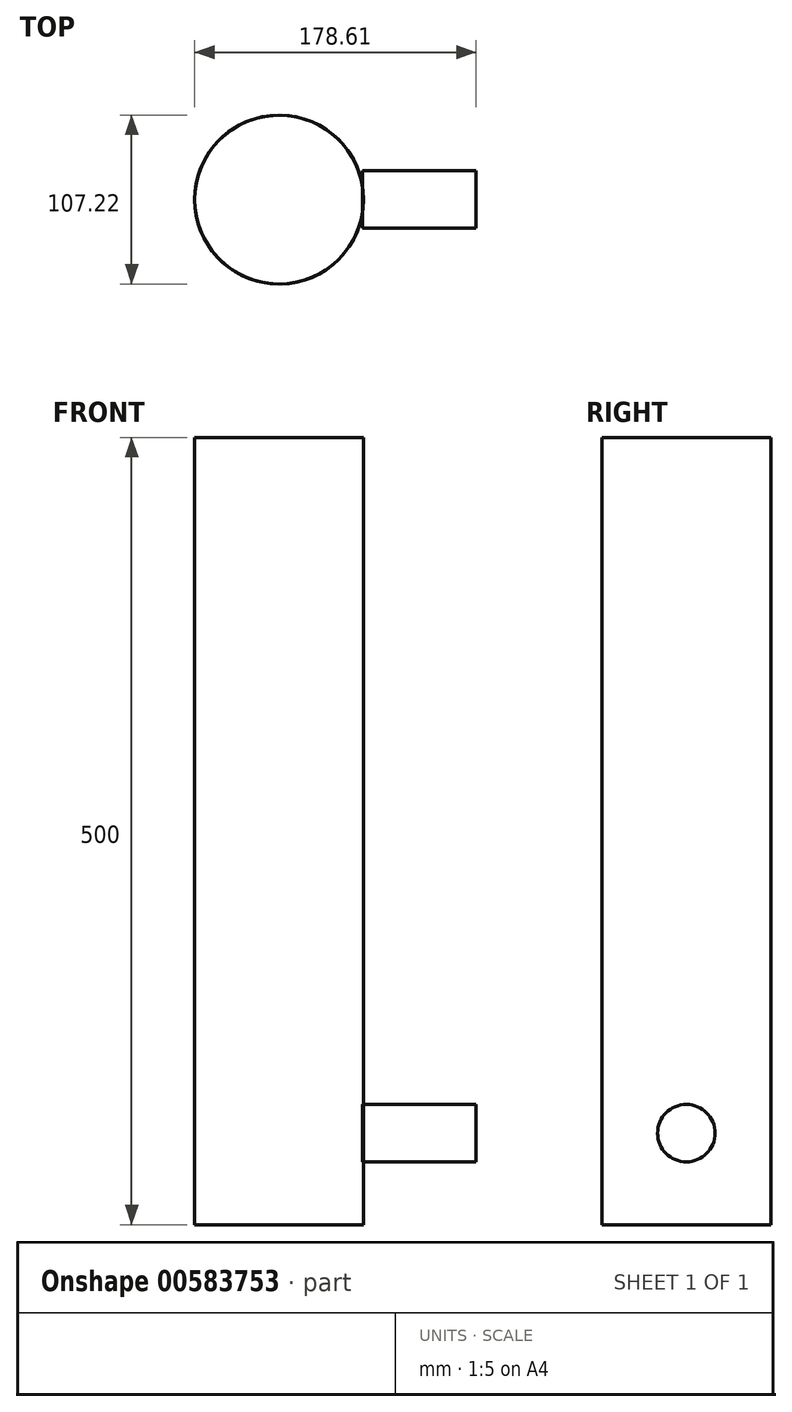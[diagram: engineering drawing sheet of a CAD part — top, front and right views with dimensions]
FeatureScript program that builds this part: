
annotation { "Feature Type Name" : "Feature", "Feature Type Description" : "" }
export const myFeature = defineFeature(function(context is Context, id is Id, definition is map)
    precondition{}
    {
        {
            var Q0;
            Q0=qCreatedBy(makeId("Top.planeOp"),FACE);
            var sketch = newSketch(context, id + "F0", { "sketchPlane" : qUnion([Q0])});
            skCircle(sketch, "E0", {"center": v(0, 0) * mm, "radius": 2.52 * mm});
            skCircle(sketch, "E1", {"center": v(0, 0) * mm, "radius": 53.6 * mm});
            skSolve(sketch);
        }
        {
            var Q0;
            Q0=makeQuery(id+"F0.imprint","IMPRINT",FACE,{"disambiguationData":[TD([[makeQuery(id+"F0.imprint","IMPRINT",EDGE,{"derivedFrom":sQuery(id+"F0.wireOp",EDGE,"E0")}),-1.0]])]});
            var Q1;
            Q1=sQuery(id+"F0.wireOp",EDGE,"E1");
            extrude(context, id + "F1", {"entities" : qUnion([Q0]), "bodyType" : ToolBodyType.SURFACE, "surfaceEntities" : qUnion([Q1]), "endBound" : BoundingType.SYMMETRIC, "depth" : 500 * mm, "offsetDistance" : 25 * mm});
        }
        {
            var Q0;
            Q0=qCreatedBy(makeId("Right.planeOp"),FACE);
            var sketch = newSketch(context, id + "F2", { "sketchPlane" : qUnion([Q0])});
            skCircle(sketch, "E2", {"center": v(0, -191.87) * mm, "radius": 18.25 * mm});
            skSolve(sketch);
        }
        {
            var Q0;
            Q0=makeQuery(id+"F2.imprint","IMPRINT",FACE,{"disambiguationData":[TD([[makeQuery(id+"F2.imprint","IMPRINT",EDGE,{"derivedFrom":sQuery(id+"F2.wireOp",EDGE,"E2")}),1.0]])]});
            var Q1;
            Q1=sQuery(id+"F2.wireOp",EDGE,"E2");
            extrude(context, id + "F3", {"entities" : qUnion([Q0]), "bodyType" : ToolBodyType.SURFACE, "surfaceEntities" : qUnion([Q1]), "depth" : 125 * mm, "offsetDistance" : 25 * mm, "hasSecondDirection" : true, "secondDirectionOppositeDirection" : false, "secondDirectionDepth" : 53 * mm, "hasSecondDirectionOffset" : true, "secondDirectionOffsetDistance" : 125 * mm});
        }
    });
